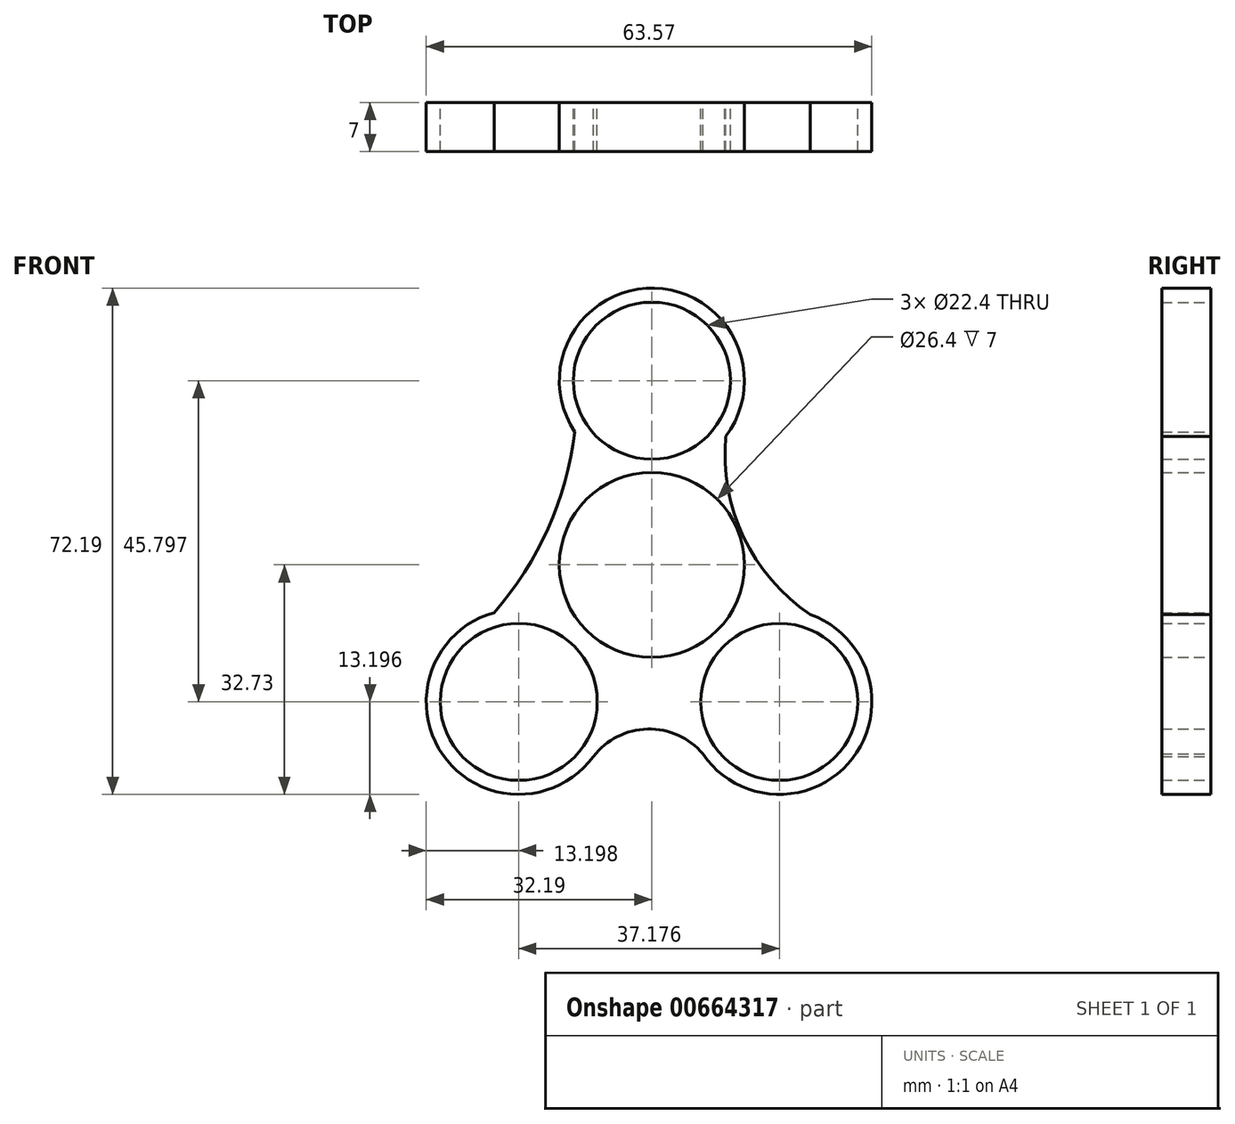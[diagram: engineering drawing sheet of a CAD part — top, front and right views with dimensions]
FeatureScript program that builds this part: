
annotation { "Feature Type Name" : "Feature", "Feature Type Description" : "" }
export const myFeature = defineFeature(function(context is Context, id is Id, definition is map)
    precondition{}
    {
        {
            var Q0;
            Q0=qCreatedBy(makeId("Front.planeOp"),FACE);
            var sketch = newSketch(context, id + "F0", { "sketchPlane" : qUnion([Q0])});
            skCircle(sketch, "E0", {"center": v(0, 0) * mm, "radius": 11.2 * mm});
            skCircle(sketch, "E1", {"center": v(0, 0) * mm, "radius": 13.2 * mm});
            skCircle(sketch, "E2", {"center": v(18.18, -19.53) * mm, "radius": 11.2 * mm});
            skCircle(sketch, "E3", {"center": v(18.18, -19.53) * mm, "radius": 13.2 * mm});
            skCircle(sketch, "E4", {"center": v(0, 26.26) * mm, "radius": 11.2 * mm});
            skCircle(sketch, "E5", {"center": v(0, 26.26) * mm, "radius": 13.2 * mm});
            skCircle(sketch, "E6", {"center": v(-19, -19.53) * mm, "radius": 11.2 * mm});
            skCircle(sketch, "E7", {"center": v(-19, -19.53) * mm, "radius": 13.2 * mm});
            skArc(sketch, "E8", {"start": v(10.54, 18.32) * mm, "mid": v(13.1, 3.96) * mm, "end": v(22.6, -7.1) * mm});
            skArc(sketch, "E9", {"start": v(-22.51, -6.81) * mm, "mid": v(-14.8, 5.2) * mm, "end": v(-11, 18.97) * mm});
            skArc(sketch, "E10", {"start": v(7.28, -26.97) * mm, "mid": v(-0.6, -23.42) * mm, "end": v(-8.33, -27.32) * mm});
            skSolve(sketch);
        }
        {
            var Q0;
            Q0 = qSketchRegion(id + "F0", true);
            extrude(context, id + "F1", {"entities" : qUnion([Q0]), "depth" : 7 * mm, "offsetDistance" : 25 * mm});
        }
    });
